# Revit family: Drain_Channel_Nero_TileInsert_80mmOutlet
name_source: partatom
category: Plumbing Fixtures
units: mm (PartAtom-declared; Revit-internal decimal feet)

## family parameters
Always vertical = Yes
Cut with Voids When Loaded = Yes
Maintain Annotation Orientation = No
OmniClass Number = 23.31.00.00
OmniClass Title = Plumbing Specific Products and Equipment
Part Type = Normal
Room Calculation Point = No
Round Connector Dimension = Use Diameter
Shared = No
Work Plane-Based = No

## types (7) — shared parameters
Assembly Code = D2010
CW Connection = Yes
HW Connection = Yes
IfcExportAs = IfcFurnitureType
IfcExportType = USERDEFINED
Manufacturer = Nero
ManufacturerOverallDepth = 106 mm
ManufacturerOverallHeight = 76 mm
ManufacturerURLProductSpecific = https://nerotapware.com.au
ModifiedIssue = 20251105 $
URL = https://nerotapware.com.au
Uniclass2015Code = Pr_65_52_24_24
Uniclass2015Title = Drainage channels with gratings
Uniclass2015Version = Products v1.35
Vent Connection = No
Waste Connection = No
zero-valued in all types: CWFU, Default Elevation, HWFU, WFU

## per-type parameters (varying)
| type | Description | ManufacturerOverallWidth | ManufacturerSpecCode | Material | Model | Type Comments |
| Brushed Gold (NRFG009HSBG) | Tile Insert V Channel 1200mm Floor Grate 80mm Outlet With Hole Saw Brushed Gold | 1200 mm  [stored 3.93701 ft] | NRFG009HSBG | Metal_Gold_Nero_Brushed | NRFG009HSBG | Drain - Channel - 80mm Outlet - Brushed Gold |
| Brushed Nickel (NRFG009HSBN) | Tile Insert V Channel 1200mm Floor Grate 80mm Outlet With Hole Saw Brushed Nickel | 1200 mm  [stored 3.93701 ft] | NRFG009HSBN | Metal_Nickel_Nero_Brushed | NRFG009HSBN | Drain - Channel - 80mm Outlet - Brushed Nickel |
| Matte Black (NRFG009HSMB) | Tile Insert V Channel 1200mm Floor Grate 80mm Outlet With Hole Saw Matte Black | 1200 mm  [stored 3.93701 ft] | NRFG009HSMB | Metal_MatteBlack_Nero | NRFG009HSMB | Drain - Channel - 80mm Outlet - Matte Black |
| Brushed Bronze (NRFG008HSBZ) | Tile Insert V Channel 600mm Floor Grate 80mm Outlet With Hole Saw Brushed Bronze | 600 mm | NRFG008HSBZ | Metal_Bronze_Nero_Brushed | NRFG008HSBZ | Drain - Channel - 80mm Outlet - Brushed Bronze |
| Brushed Nickel (NRFG008HSBN) | Tile Insert V Channel 600mm Floor Grate 80mm Outlet With Hole Saw Brushed Nickel | 600 mm | NRFG008HSBN | Metal_Nickel_Nero_Brushed | NRFG008HSBN | Drain - Channel - 80mm Outlet - Brushed Nickel |
| Brushed Gold (NRFG008HSBG) | Tile Insert V Channel 600mm Floor Grate 80mm Outlet With Hole Saw Brushed Gold | 600 mm | NRFG008HSBG | Metal_Gold_Nero_Brushed | NRFG008HSBG | Drain - Channel - 80mm Outlet - Brushed Gold |
| Matte Black (NRFG008HSMB) | Tile Insert V Channel 600mm Floor Grate 80mm Outlet With Hole Saw Matte Black | 600 mm | NRFG008HSMB | Metal_MatteBlack_Nero | NRFG008HSMB | Drain - Channel - 80mm Outlet - Matte Black |

note: [stored X ft] marks values corroborated as IEEE doubles in the binary element streams (Revit-internal decimal feet)

## geometry (parser evidence)
native form markers: Sweep x2
no freeform markers — native parametric forms only
